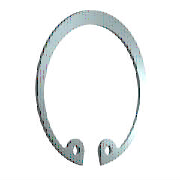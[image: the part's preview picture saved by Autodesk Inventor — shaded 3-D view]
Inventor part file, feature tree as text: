
AUTODESK INVENTOR PART (.ipt)
format: ipt  version: 2025 (Build 290162010, 162A)  size: 164,352 bytes
history: native  units: mm (DEFAULTED — no unit token found)
features: plane x3, other x2, hole x2, sketch x1
ambient origin geometry x8: Origin, YZ Plane, XZ Plane, XY Plane, X Axis, Y Axis, Z Axis, Center Point
bodies: Solid1 (feature_tree)
feature tree (8):
  plane  "WorkPlane1"
  plane  "Work Plane2"
  plane  "WorkPlane2"
  sketch  "Sketch1"  dims[d0=-1.6mm d1=5.2mm d2=21.2mm d3=0.0mm d4=0.0mm d5=4.227778mm d6=18.927778mm d7=0.283333mm d8=0.983333mm d9=3.12mm d10=6.5mm d11=3.12mm d12=6.5mm d13=1.08mm d14=2.25mm d15=1.08mm d16=2.25mm d17=3.66mm d18=18.65mm d19=3.66mm d20=18.65mm d21=6.283185mm d22=6.283185mm d23=6.283185mm d24=6.283185mm d25=1.6mm d26=0.0mm d27=0.0mm d28=0.0mm d29=2.5mm d30=6.0mm d31=4.0mm d32=2.0mm d33=60.0deg d34=8.0mm d35=20.594885mm d36=2.5mm d37=6.0mm d38=4.0mm d39=2.0mm d40=60.0deg d41=8.0mm d42=20.594885mm d47=0.0mm d48=0.0mm d49=0.0mm d50=0.0mm]
  other  "WorkPoint1"
  other  "WorkAxis1"
  hole  "Hole1"  [1 undecoded]
  hole  "Hole2"  [1 undecoded]
note: 2 required parameter values undecoded (feature->parameter linkage not recoverable at this tier; creation-order binding heuristic only, values carry confidence <= 0.55)
